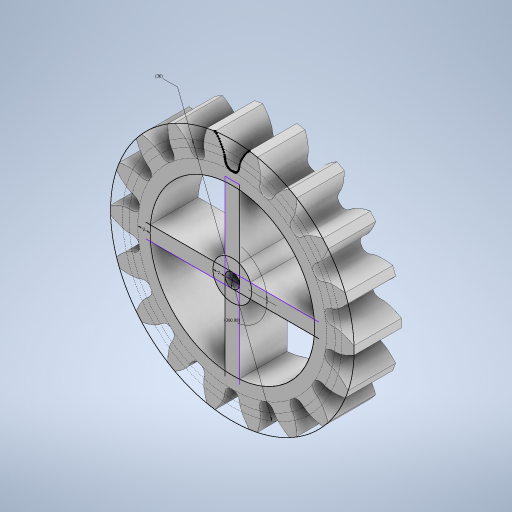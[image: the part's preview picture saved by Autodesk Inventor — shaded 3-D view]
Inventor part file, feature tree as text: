
AUTODESK INVENTOR PART (.ipt)
format: ipt  version: 2023 (Build 270158000, 158)  size: 428,544 bytes
history: native  units: mm
features: extrude x3, sketch x1, pattern_circular x1
ambient origin geometry x8: Origin, YZ Plane, XZ Plane, XY Plane, X Axis, Y Axis, Z Axis, Center Point
bodies: Solid1 (feature_tree)
feature tree (5):
  sketch  "Sketch1"  dims[d0=7.82mm d1=0.0mm d2=0.0mm d3=0.0mm d4=180.0mm d5=360.0deg d7=2.37mm d8=0.0mm d9=0.0mm d10=36.0mm d11=2.0mm d12=2.0mm d13=40.0mm d15=360.0deg d17=0.5mm d18=0.872665mm d19=0.5mm d20=0.872665mm]
  extrude  "Extrusion1"  TaperAngle=0.0deg  [1 undecoded]
  extrude  "Extrusion2"  Depth=2.37mm TaperAngle=360.0deg
  pattern_circular  "Circular Pattern1"  [2 undecoded]
  extrude  "Extrusion3"  TaperAngle=0.0deg  [1 undecoded]
note: 4 required parameter values undecoded (feature->parameter linkage not recoverable at this tier; creation-order binding heuristic only, values carry confidence <= 0.55)
